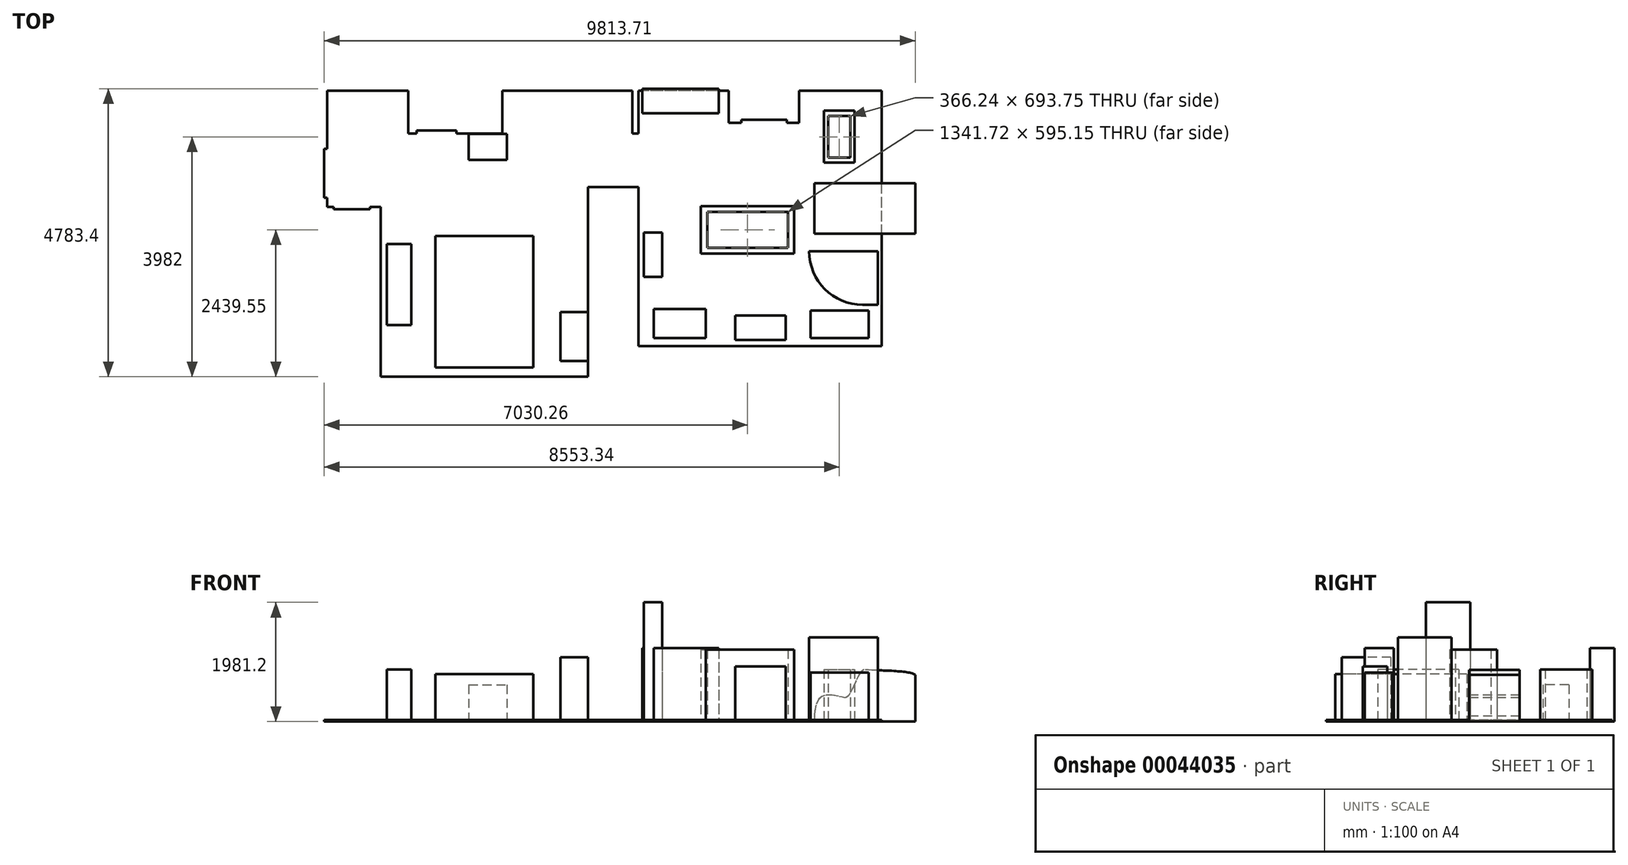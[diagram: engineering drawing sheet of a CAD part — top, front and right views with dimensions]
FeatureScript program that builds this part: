
annotation { "Feature Type Name" : "Feature", "Feature Type Description" : "" }
export const myFeature = defineFeature(function(context is Context, id is Id, definition is map)
    precondition{}
    {
        {
            var Q0;
            Q0=qCreatedBy(makeId("Top.planeOp"),FACE);
            var sketch = newSketch(context, id + "F0", { "sketchPlane" : qUnion([Q0])});
            skLineSegment(sketch, "E0.bottom", {"start": v(0, 0) * mm, "end": v(-101.6, 0) * mm});
            skLineSegment(sketch, "E0.top", {"start": v(0, 2819.4) * mm, "end": v(-101.6, 2819.4) * mm});
            skLineSegment(sketch, "E0.left", {"start": v(0, 0) * mm, "end": v(0, 2819.4) * mm});
            skLineSegment(sketch, "E0.right", {"start": v(-101.6, 0) * mm, "end": v(-101.6, 2819.4) * mm});
            skLineSegment(sketch, "E1.bottom", {"start": v(0, 0) * mm, "end": v(3441.7, 0) * mm});
            skLineSegment(sketch, "E1.top", {"start": v(0, -101.6) * mm, "end": v(3441.7, -101.6) * mm});
            skLineSegment(sketch, "E1.left", {"start": v(0, 0) * mm, "end": v(0, -101.6) * mm});
            skLineSegment(sketch, "E1.right", {"start": v(3441.7, 0) * mm, "end": v(3441.7, -101.6) * mm});
            skLineSegment(sketch, "E2.bottom", {"start": v(1485.9, 4140.2) * mm, "end": v(1917.7, 4140.2) * mm});
            skLineSegment(sketch, "E2.top", {"start": v(1485.9, 4572) * mm, "end": v(1917.7, 4572) * mm});
            skLineSegment(sketch, "E2.left", {"start": v(1485.9, 4140.2) * mm, "end": v(1485.9, 4572) * mm});
            skLineSegment(sketch, "E2.right", {"start": v(1917.7, 4140.2) * mm, "end": v(1917.7, 4572) * mm});
            skLineSegment(sketch, "E3.bottom", {"start": v(0, 2819.4) * mm, "end": v(-181.25, 2819.4) * mm});
            skLineSegment(sketch, "E3.top", {"start": v(0, 2717.8) * mm, "end": v(-990.6, 2717.8) * mm});
            skLineSegment(sketch, "E3.left", {"start": v(0, 2819.4) * mm, "end": v(0, 2717.8) * mm});
            skLineSegment(sketch, "E3.right", {"start": v(-990.6, 2819.4) * mm, "end": v(-990.6, 2717.8) * mm});
            skLineSegment(sketch, "E4.bottom", {"start": v(-990.6, 2819.4) * mm, "end": v(-889, 2819.4) * mm});
            skLineSegment(sketch, "E4.top", {"start": v(-990.6, 4495.8) * mm, "end": v(-889, 4495.8) * mm});
            skLineSegment(sketch, "E4.left", {"start": v(-990.6, 2819.4) * mm, "end": v(-990.6, 4495.8) * mm});
            skLineSegment(sketch, "E4.right", {"start": v(-889, 2819.4) * mm, "end": v(-889, 2971.8) * mm});
            skLineSegment(sketch, "E5", {"start": v(1701.8, 4140.2) * mm, "end": v(1701.8, 4749.8) * mm, "construction": true});
            skLineSegment(sketch, "E6", {"start": v(1701.8, 4749.8) * mm, "end": v(-889, 4749.8) * mm, "construction": true});
            skLineSegment(sketch, "E7.bottom", {"start": v(-889, 4495.8) * mm, "end": v(-990.6, 4495.8) * mm});
            skLineSegment(sketch, "E7.top", {"start": v(-889, 4749.8) * mm, "end": v(-990.6, 4749.8) * mm});
            skLineSegment(sketch, "E7.left", {"start": v(-889, 4495.8) * mm, "end": v(-889, 4749.8) * mm});
            skLineSegment(sketch, "E7.right", {"start": v(-990.6, 4495.8) * mm, "end": v(-990.6, 4749.8) * mm});
            skLineSegment(sketch, "E8.bottom", {"start": v(3441.7, 0) * mm, "end": v(3543.3, 0) * mm});
            skLineSegment(sketch, "E8.top", {"start": v(3441.7, 3149.6) * mm, "end": v(3543.3, 3149.6) * mm});
            skLineSegment(sketch, "E8.left", {"start": v(3441.7, 0) * mm, "end": v(3441.7, 3149.6) * mm});
            skLineSegment(sketch, "E8.right", {"start": v(3543.3, 0) * mm, "end": v(3543.3, 3149.6) * mm});
            skLineSegment(sketch, "E9.bottom", {"start": v(3441.7, 3149.6) * mm, "end": v(4279.9, 3149.6) * mm});
            skLineSegment(sketch, "E9.top", {"start": v(3441.7, 3048) * mm, "end": v(4279.9, 3048) * mm});
            skLineSegment(sketch, "E9.left", {"start": v(3441.7, 3149.6) * mm, "end": v(3441.7, 3048) * mm});
            skLineSegment(sketch, "E9.right", {"start": v(4279.9, 3149.6) * mm, "end": v(4279.9, 3048) * mm});
            skLineSegment(sketch, "E10", {"start": v(0, 0) * mm, "end": v(8318.5, 0) * mm, "construction": true});
            skLineSegment(sketch, "E11.bottom", {"start": v(4279.9, 3149.6) * mm, "end": v(4178.3, 3149.6) * mm});
            skLineSegment(sketch, "E11.top", {"start": v(4298.95, 0) * mm, "end": v(4178.3, 0) * mm});
            skLineSegment(sketch, "E11.left", {"start": v(4279.9, 3149.6) * mm, "end": v(4279.9, 406.4) * mm});
            skLineSegment(sketch, "E11.right", {"start": v(4178.3, 3149.6) * mm, "end": v(4178.3, 406.4) * mm});
            skLineSegment(sketch, "E12.bottom", {"start": v(4298.95, 0) * mm, "end": v(8337.55, 0) * mm});
            skLineSegment(sketch, "E13.bottom", {"start": v(3505.2, 1168.4) * mm, "end": v(3937, 1168.4) * mm});
            skLineSegment(sketch, "E13.top", {"start": v(3505.2, 736.6) * mm, "end": v(3937, 736.6) * mm});
            skLineSegment(sketch, "E13.left", {"start": v(3505.2, 1168.4) * mm, "end": v(3505.2, 736.6) * mm});
            skLineSegment(sketch, "E13.right", {"start": v(3937, 1168.4) * mm, "end": v(3937, 736.6) * mm});
            skLineSegment(sketch, "E14.bottom", {"start": v(4279.9, 508) * mm, "end": v(8318.5, 508) * mm});
            skLineSegment(sketch, "E14.top", {"start": v(4279.9, 406.4) * mm, "end": v(8318.5, 406.4) * mm});
            skLineSegment(sketch, "E14.left", {"start": v(4279.9, 508) * mm, "end": v(4279.9, 406.4) * mm});
            skLineSegment(sketch, "E14.right", {"start": v(8318.5, 508) * mm, "end": v(8318.5, 406.4) * mm});
            skLineSegment(sketch, "E15", {"start": v(4279.9, 406.4) * mm, "end": v(4178.3, 406.4) * mm});
            skLineSegment(sketch, "E16.bottom", {"start": v(8318.5, 508) * mm, "end": v(8420.1, 508) * mm});
            skLineSegment(sketch, "E16.top", {"start": v(8318.5, 4749.8) * mm, "end": v(8420.1, 4749.8) * mm});
            skLineSegment(sketch, "E16.left", {"start": v(8318.5, 508) * mm, "end": v(8318.5, 4749.8) * mm});
            skLineSegment(sketch, "E16.right", {"start": v(8420.1, 508) * mm, "end": v(8420.1, 4749.8) * mm});
            skLineSegment(sketch, "E17.bottom", {"start": v(8318.5, 4749.8) * mm, "end": v(6946.9, 4749.8) * mm});
            skLineSegment(sketch, "E17.top", {"start": v(8318.5, 4851.4) * mm, "end": v(6946.9, 4851.4) * mm});
            skLineSegment(sketch, "E17.left", {"start": v(8318.5, 4749.8) * mm, "end": v(8318.5, 4851.4) * mm});
            skLineSegment(sketch, "E17.right", {"start": v(6946.9, 4749.8) * mm, "end": v(6946.9, 4851.4) * mm});
            skLineSegment(sketch, "E18.bottom", {"start": v(6946.9, 4749.8) * mm, "end": v(6845.3, 4749.8) * mm});
            skLineSegment(sketch, "E18.top", {"start": v(6946.9, 4216.4) * mm, "end": v(6845.3, 4216.4) * mm});
            skLineSegment(sketch, "E18.left", {"start": v(6946.9, 4749.8) * mm, "end": v(6946.9, 4216.4) * mm});
            skLineSegment(sketch, "E18.right", {"start": v(6845.3, 4749.8) * mm, "end": v(6845.3, 4216.4) * mm});
            skLineSegment(sketch, "E19.bottom", {"start": v(6845.3, 4216.4) * mm, "end": v(6744.88, 4216.4) * mm});
            skLineSegment(sketch, "E19.top", {"start": v(6845.3, 4318) * mm, "end": v(5778.5, 4318) * mm});
            skLineSegment(sketch, "E19.left", {"start": v(6845.3, 4216.4) * mm, "end": v(6845.3, 4318) * mm});
            skLineSegment(sketch, "E19.right", {"start": v(5778.5, 4216.4) * mm, "end": v(5778.5, 4318) * mm});
            skLineSegment(sketch, "E20.bottom", {"start": v(5778.5, 4216.4) * mm, "end": v(5880.1, 4216.4) * mm});
            skLineSegment(sketch, "E20.top", {"start": v(5778.5, 4749.8) * mm, "end": v(5880.1, 4749.8) * mm});
            skLineSegment(sketch, "E20.left", {"start": v(5778.5, 4216.4) * mm, "end": v(5778.5, 4749.8) * mm});
            skLineSegment(sketch, "E20.right", {"start": v(5880.1, 4216.4) * mm, "end": v(5880.1, 4749.8) * mm});
            skLineSegment(sketch, "E21.bottom", {"start": v(5778.5, 4749.8) * mm, "end": v(4279.9, 4749.8) * mm});
            skLineSegment(sketch, "E21.top", {"start": v(5778.5, 4851.4) * mm, "end": v(4279.9, 4851.4) * mm});
            skLineSegment(sketch, "E21.left", {"start": v(5778.5, 4749.8) * mm, "end": v(5778.5, 4851.4) * mm});
            skLineSegment(sketch, "E21.right", {"start": v(4279.9, 4749.8) * mm, "end": v(4279.9, 4851.4) * mm});
            skLineSegment(sketch, "E22.bottom", {"start": v(-889, 4749.8) * mm, "end": v(4178.3, 4749.8) * mm});
            skLineSegment(sketch, "E22.top", {"start": v(-889, 4851.4) * mm, "end": v(4178.3, 4851.4) * mm});
            skLineSegment(sketch, "E22.left", {"start": v(-889, 4749.8) * mm, "end": v(-889, 4851.4) * mm});
            skLineSegment(sketch, "E22.right", {"start": v(4178.3, 4749.8) * mm, "end": v(4178.3, 4851.4) * mm});
            skLineSegment(sketch, "E23.bottom", {"start": v(4279.9, 4851.4) * mm, "end": v(4178.3, 4851.4) * mm});
            skLineSegment(sketch, "E23.top", {"start": v(4279.9, 4038.6) * mm, "end": v(4178.3, 4038.6) * mm});
            skLineSegment(sketch, "E23.left", {"start": v(4279.9, 4851.4) * mm, "end": v(4279.9, 4038.6) * mm});
            skLineSegment(sketch, "E23.right", {"start": v(4178.3, 4851.4) * mm, "end": v(4178.3, 4038.6) * mm});
            skLineSegment(sketch, "E24", {"start": v(1798.14, 4140.2) * mm, "end": v(1798.14, 4038.6) * mm, "construction": true});
            skLineSegment(sketch, "E25", {"start": v(1798.14, 4038.6) * mm, "end": v(4178.3, 4038.6) * mm, "construction": true});
            skLineSegment(sketch, "E26", {"start": v(4178.3, 4038.6) * mm, "end": v(1798.14, 4038.6) * mm, "construction": true});
            skLineSegment(sketch, "E27", {"start": v(1798.14, 4038.6) * mm, "end": v(-889, 4038.6) * mm, "construction": true});
            skLineSegment(sketch, "E28.bottom", {"start": v(1397, 4749.8) * mm, "end": v(1485.9, 4749.8) * mm});
            skLineSegment(sketch, "E28.top", {"start": v(1397, 4038.6) * mm, "end": v(1485.9, 4038.6) * mm});
            skLineSegment(sketch, "E28.left", {"start": v(1397, 4749.8) * mm, "end": v(1397, 4038.6) * mm});
            skLineSegment(sketch, "E28.right", {"start": v(1485.9, 4749.8) * mm, "end": v(1485.9, 4038.6) * mm});
            skLineSegment(sketch, "E29.bottom", {"start": v(1917.7, 4749.8) * mm, "end": v(2019.3, 4749.8) * mm});
            skLineSegment(sketch, "E29.top", {"start": v(1917.7, 4038.6) * mm, "end": v(2019.3, 4038.6) * mm});
            skLineSegment(sketch, "E29.left", {"start": v(1917.7, 4749.8) * mm, "end": v(1917.7, 4038.6) * mm});
            skLineSegment(sketch, "E29.right", {"start": v(2019.3, 4749.8) * mm, "end": v(2019.3, 4038.6) * mm});
            skLineSegment(sketch, "E30.bottom", {"start": v(1397, 4038.6) * mm, "end": v(2019.3, 4038.6) * mm});
            skLineSegment(sketch, "E30.top", {"start": v(1397, 4140.2) * mm, "end": v(2019.3, 4140.2) * mm});
            skLineSegment(sketch, "E30.left", {"start": v(1397, 4038.6) * mm, "end": v(1397, 4140.2) * mm});
            skLineSegment(sketch, "E30.right", {"start": v(2019.3, 4038.6) * mm, "end": v(2019.3, 4140.2) * mm});
            skLineSegment(sketch, "E31.bottom", {"start": v(1295.4, 4038.6) * mm, "end": v(1257.3, 4038.6) * mm});
            skLineSegment(sketch, "E31.top", {"start": v(1295.4, 4140.2) * mm, "end": v(1257.3, 4140.2) * mm});
            skLineSegment(sketch, "E31.left", {"start": v(1295.4, 4038.6) * mm, "end": v(1295.4, 4140.2) * mm});
            skLineSegment(sketch, "E31.right", {"start": v(1257.3, 4038.6) * mm, "end": v(1257.3, 4140.2) * mm});
            skLineSegment(sketch, "E32.bottom", {"start": v(558.8, 4038.6) * mm, "end": v(596.9, 4038.6) * mm});
            skLineSegment(sketch, "E32.top", {"start": v(558.8, 4140.2) * mm, "end": v(596.9, 4140.2) * mm});
            skLineSegment(sketch, "E32.left", {"start": v(558.8, 4038.6) * mm, "end": v(558.8, 4140.2) * mm});
            skLineSegment(sketch, "E32.right", {"start": v(596.9, 4038.6) * mm, "end": v(596.9, 4140.2) * mm});
            skLineSegment(sketch, "E33.bottom", {"start": v(558.8, 4038.6) * mm, "end": v(457.2, 4038.6) * mm});
            skLineSegment(sketch, "E33.top", {"start": v(558.8, 4749.8) * mm, "end": v(457.2, 4749.8) * mm});
            skLineSegment(sketch, "E33.left", {"start": v(558.8, 4038.6) * mm, "end": v(558.8, 4749.8) * mm});
            skLineSegment(sketch, "E33.right", {"start": v(457.2, 4038.6) * mm, "end": v(457.2, 4749.8) * mm});
            skLineSegment(sketch, "E34", {"start": v(1295.4, 4038.6) * mm, "end": v(1397, 4038.6) * mm});
            skLineSegment(sketch, "E35", {"start": v(596.9, 4089.4) * mm, "end": v(1257.3, 4089.4) * mm});
            skLineSegment(sketch, "E36", {"start": v(5984.67, 4216.4) * mm, "end": v(5984.67, 4267.2) * mm});
            skPoint(sketch, "E36.endSnap0", {"position": v(5778.5, 4267.2) * mm});
            skLineSegment(sketch, "E37", {"start": v(5984.67, 4267.2) * mm, "end": v(6744.88, 4267.2) * mm});
            skLineSegment(sketch, "E38", {"start": v(6744.88, 4267.2) * mm, "end": v(6744.88, 4216.4) * mm});
            skLineSegment(sketch, "E39.trimOffspring", {"start": v(5984.67, 4216.4) * mm, "end": v(5778.5, 4216.4) * mm});
            skLineSegment(sketch, "E40", {"start": v(-784.2, 2819.4) * mm, "end": v(-784.2, 2780.53) * mm});
            skLineSegment(sketch, "E41", {"start": v(-784.2, 2780.53) * mm, "end": v(-181.25, 2782.63) * mm});
            skLineSegment(sketch, "E42", {"start": v(-181.25, 2782.63) * mm, "end": v(-181.25, 2819.4) * mm});
            skLineSegment(sketch, "E43.trimOffspring", {"start": v(-784.2, 2819.4) * mm, "end": v(-990.6, 2819.4) * mm});
            skLineSegment(sketch, "E44", {"start": v(-889, 2971.8) * mm, "end": v(-939.8, 2971.8) * mm});
            skLineSegment(sketch, "E45", {"start": v(-939.8, 2971.8) * mm, "end": v(-939.8, 3784.6) * mm});
            skLineSegment(sketch, "E46", {"start": v(-939.8, 3784.6) * mm, "end": v(-889, 3784.6) * mm});
            skLineSegment(sketch, "E47.trimOffspring", {"start": v(-889, 3784.6) * mm, "end": v(-889, 4495.8) * mm});
            skSolve(sketch);
        }
        {
            var Q0;
            Q0=makeQuery(id+"F0.imprint","IMPRINT",FACE,{"disambiguationData":[TD([[makeQuery(id+"F0.imprint","IMPRINT",EDGE,{"derivedFrom":sQuery(id+"F0.wireOp",EDGE,"E0.left")}),-1.0]])]});
            extrude(context, id + "F1", {"entities" : qUnion([Q0]), "depth" : 25.4 * mm});
        }
        {
            var Q0;
            Q0=makeQuery(id+"F1.opExtrude","CAP_FACE",FACE,{"disambiguationData":[OSD([sQuery(id+"F0.wireOp",EDGE,"E0.left"),sQuery(id+"F0.wireOp",EDGE,"E1.bottom"),sQuery(id+"F0.wireOp",EDGE,"E2.bottom"),sQuery(id+"F0.wireOp",EDGE,"E2.top"),sQuery(id+"F0.wireOp",EDGE,"E2.left"),sQuery(id+"F0.wireOp",EDGE,"E2.right"),sQuery(id+"F0.wireOp",EDGE,"E3.bottom"),sQuery(id+"F0.wireOp",EDGE,"E3.left"),sQuery(id+"F0.wireOp",EDGE,"E4.right"),sQuery(id+"F0.wireOp",EDGE,"E7.left"),sQuery(id+"F0.wireOp",EDGE,"E8.left"),sQuery(id+"F0.wireOp",EDGE,"E9.bottom"),sQuery(id+"F0.wireOp",EDGE,"E9.left"),sQuery(id+"F0.wireOp",EDGE,"E11.bottom"),sQuery(id+"F0.wireOp",EDGE,"E11.left"),sQuery(id+"F0.wireOp",EDGE,"E14.bottom"),sQuery(id+"F0.wireOp",EDGE,"E16.left"),sQuery(id+"F0.wireOp",EDGE,"E17.bottom"),sQuery(id+"F0.wireOp",EDGE,"E18.top"),sQuery(id+"F0.wireOp",EDGE,"E18.left"),sQuery(id+"F0.wireOp",EDGE,"E19.bottom"),sQuery(id+"F0.wireOp",EDGE,"E20.bottom"),sQuery(id+"F0.wireOp",EDGE,"E20.left"),sQuery(id+"F0.wireOp",EDGE,"E21.bottom"),sQuery(id+"F0.wireOp",EDGE,"E22.bottom"),sQuery(id+"F0.wireOp",EDGE,"E23.top"),sQuery(id+"F0.wireOp",EDGE,"E23.left"),sQuery(id+"F0.wireOp",EDGE,"E23.right")])],"isStart":false});
            var sketch = newSketch(context, id + "F2", { "sketchPlane" : qUnion([Q0])});
            skLineSegment(sketch, "E48.bottom", {"start": v(908.05, 2336.8) * mm, "end": v(2533.65, 2336.8) * mm});
            skLineSegment(sketch, "E48.top", {"start": v(908.05, 152.4) * mm, "end": v(2533.65, 152.4) * mm});
            skLineSegment(sketch, "E48.left", {"start": v(908.05, 2336.8) * mm, "end": v(908.05, 152.4) * mm});
            skLineSegment(sketch, "E48.right", {"start": v(2533.65, 2336.8) * mm, "end": v(2533.65, 152.4) * mm});
            skLineSegment(sketch, "E49.0", {"start": v(0, 0) * mm, "end": v(3441.7, 0) * mm});
            skPoint(sketch, "E50", {"position": v(1720.85, 0) * mm});
            skPoint(sketch, "E51", {"position": v(1720.85, 152.4) * mm});
            skSolve(sketch);
        }
        {
            var Q0;
            Q0 = qSketchRegion(id + "F2", true);
            extrude(context, id + "F3", {"entities" : qUnion([Q0]), "depth" : 762 * mm});
        }
        {
            var Q0;
            Q0=qCreatedBy(makeId("Top.planeOp"),FACE);
            var sketch = newSketch(context, id + "F4", { "sketchPlane" : qUnion([Q0])});
            skLineSegment(sketch, "E52.bottom", {"start": v(4339.31, 4783.4) * mm, "end": v(5609.31, 4783.4) * mm});
            skLineSegment(sketch, "E52.top", {"start": v(4339.31, 4377) * mm, "end": v(5609.31, 4377) * mm});
            skLineSegment(sketch, "E52.left", {"start": v(4339.31, 4783.4) * mm, "end": v(4339.31, 4377) * mm});
            skLineSegment(sketch, "E52.right", {"start": v(5609.31, 4783.4) * mm, "end": v(5609.31, 4377) * mm});
            skSolve(sketch);
        }
        {
            var Q0;
            Q0 = qSketchRegion(id + "F4", true);
            extrude(context, id + "F5", {"entities" : qUnion([Q0]), "depth" : 1219.2 * mm});
        }
        {
            var Q0;
            Q0=qCreatedBy(makeId("Top.planeOp"),FACE);
            var sketch = newSketch(context, id + "F6", { "sketchPlane" : qUnion([Q0])});
            skLineSegment(sketch, "E53.bottom", {"start": v(8104.33, 639.74) * mm, "end": v(7139.13, 639.74) * mm});
            skLineSegment(sketch, "E53.top", {"start": v(8104.33, 1096.94) * mm, "end": v(7139.13, 1096.94) * mm});
            skLineSegment(sketch, "E53.left", {"start": v(8104.33, 639.74) * mm, "end": v(8104.33, 1096.94) * mm});
            skLineSegment(sketch, "E53.right", {"start": v(7139.13, 639.74) * mm, "end": v(7139.13, 1096.94) * mm});
            skSolve(sketch);
        }
        {
            var Q0;
            Q0 = qSketchRegion(id + "F6", true);
            extrude(context, id + "F7", {"entities" : qUnion([Q0]), "depth" : 812.8 * mm});
        }
        {
            var Q0;
            Q0=qCreatedBy(makeId("Top.planeOp"),FACE);
            var sketch = newSketch(context, id + "F8", { "sketchPlane" : qUnion([Q0])});
            skLineSegment(sketch, "E54.bottom", {"start": v(8255.57, 1194.17) * mm, "end": v(8001.57, 1194.17) * mm});
            skLineSegment(sketch, "E54.top", {"start": v(8255.57, 2083.17) * mm, "end": v(8001.57, 2083.17) * mm});
            skLineSegment(sketch, "E54.left", {"start": v(8255.57, 1194.17) * mm, "end": v(8255.57, 2083.17) * mm});
            skLineSegment(sketch, "E54.right", {"start": v(8001.57, 1194.17) * mm, "end": v(8001.57, 2083.17) * mm});
            skLineSegment(sketch, "E55", {"start": v(8255.57, 2083.17) * mm, "end": v(7112.57, 2083.17) * mm});
            skArc(sketch, "E56", {"start": v(7112.57, 2083.17) * mm, "mid": v(7372.95, 1454.55) * mm, "end": v(8001.57, 1194.17) * mm});
            skSolve(sketch);
        }
        {
            var Q0;
            Q0 = qSketchRegion(id + "F8", true);
            extrude(context, id + "F9", {"entities" : qUnion([Q0]), "depth" : 1397 * mm});
        }
        {
            var Q0;
            Q0=qCreatedBy(makeId("Top.planeOp"),FACE);
            var sketch = newSketch(context, id + "F10", { "sketchPlane" : qUnion([Q0])});
            skLineSegment(sketch, "E57.bottom", {"start": v(4531.26, 639.74) * mm, "end": v(5394.86, 639.74) * mm});
            skLineSegment(sketch, "E57.top", {"start": v(4531.26, 1122.34) * mm, "end": v(5394.86, 1122.34) * mm});
            skLineSegment(sketch, "E57.left", {"start": v(4531.26, 639.74) * mm, "end": v(4531.26, 1122.34) * mm});
            skLineSegment(sketch, "E57.right", {"start": v(5394.86, 639.74) * mm, "end": v(5394.86, 1122.34) * mm});
            skSolve(sketch);
        }
        {
            var Q0;
            Q0 = qSketchRegion(id + "F10", true);
            extrude(context, id + "F11", {"entities" : qUnion([Q0]), "depth" : 1219.2 * mm});
        }
        {
            var Q0;
            Q0=qCreatedBy(makeId("Top.planeOp"),FACE);
            var sketch = newSketch(context, id + "F12", { "sketchPlane" : qUnion([Q0])});
            skLineSegment(sketch, "E58.bottom", {"start": v(1460.8, 4028.5) * mm, "end": v(2095.8, 4028.5) * mm});
            skLineSegment(sketch, "E58.top", {"start": v(1460.8, 3596.7) * mm, "end": v(2095.8, 3596.7) * mm});
            skLineSegment(sketch, "E58.left", {"start": v(1460.8, 4028.5) * mm, "end": v(1460.8, 3596.7) * mm});
            skLineSegment(sketch, "E58.right", {"start": v(2095.8, 4028.5) * mm, "end": v(2095.8, 3596.7) * mm});
            skSolve(sketch);
        }
        {
            var Q0;
            Q0 = qSketchRegion(id + "F12", true);
            extrude(context, id + "F13", {"entities" : qUnion([Q0]), "depth" : 609.6 * mm});
        }
        {
            var Q0;
            Q0=qCreatedBy(makeId("Top.planeOp"),FACE);
            var sketch = newSketch(context, id + "F14", { "sketchPlane" : qUnion([Q0])});
            skLineSegment(sketch, "E59.bottom", {"start": v(4370.2, 2392.8) * mm, "end": v(4675, 2392.8) * mm});
            skLineSegment(sketch, "E59.top", {"start": v(4370.2, 1656.2) * mm, "end": v(4675, 1656.2) * mm});
            skLineSegment(sketch, "E59.left", {"start": v(4370.2, 2392.8) * mm, "end": v(4370.2, 1656.2) * mm});
            skLineSegment(sketch, "E59.right", {"start": v(4675, 2392.8) * mm, "end": v(4675, 1656.2) * mm});
            skSolve(sketch);
        }
        {
            var Q0;
            Q0 = qSketchRegion(id + "F14", true);
            extrude(context, id + "F15", {"entities" : qUnion([Q0]), "depth" : 1981.2 * mm});
        }
        {
            var Q0;
            Q0=qCreatedBy(makeId("Top.planeOp"),FACE);
            var sketch = newSketch(context, id + "F16", { "sketchPlane" : qUnion([Q0])});
            skLineSegment(sketch, "E60.bottom", {"start": v(3438.11, 1072.66) * mm, "end": v(2980.91, 1072.66) * mm});
            skLineSegment(sketch, "E60.top", {"start": v(3438.11, 259.86) * mm, "end": v(2980.91, 259.86) * mm});
            skLineSegment(sketch, "E60.left", {"start": v(3438.11, 1072.66) * mm, "end": v(3438.11, 259.86) * mm});
            skLineSegment(sketch, "E60.right", {"start": v(2980.91, 1072.66) * mm, "end": v(2980.91, 259.86) * mm});
            skSolve(sketch);
        }
        {
            var Q0;
            Q0 = qSketchRegion(id + "F16", true);
            extrude(context, id + "F17", {"entities" : qUnion([Q0]), "depth" : 1066.8 * mm});
        }
        {
            var Q0;
            Q0=qCreatedBy(makeId("Top.planeOp"),FACE);
            var sketch = newSketch(context, id + "F18", { "sketchPlane" : qUnion([Q0])});
            skLineSegment(sketch, "E61.bottom", {"start": v(100.12, 2201.56) * mm, "end": v(506.52, 2201.56) * mm});
            skLineSegment(sketch, "E61.top", {"start": v(100.12, 855.36) * mm, "end": v(506.52, 855.36) * mm});
            skLineSegment(sketch, "E61.left", {"start": v(100.12, 2201.56) * mm, "end": v(100.12, 855.36) * mm});
            skLineSegment(sketch, "E61.right", {"start": v(506.52, 2201.56) * mm, "end": v(506.52, 855.36) * mm});
            skSolve(sketch);
        }
        {
            var Q0;
            Q0 = qSketchRegion(id + "F18", true);
            extrude(context, id + "F19", {"entities" : qUnion([Q0]), "depth" : 863.6 * mm});
        }
        {
            var Q0;
            Q0=qCreatedBy(makeId("Top.planeOp"),FACE);
            var sketch = newSketch(context, id + "F20", { "sketchPlane" : qUnion([Q0])});
            skLineSegment(sketch, "E62.bottom", {"start": v(5886.53, 1015.34) * mm, "end": v(6724.73, 1015.34) * mm});
            skLineSegment(sketch, "E62.top", {"start": v(5886.53, 608.94) * mm, "end": v(6724.73, 608.94) * mm});
            skLineSegment(sketch, "E62.left", {"start": v(5886.53, 1015.34) * mm, "end": v(5886.53, 608.94) * mm});
            skLineSegment(sketch, "E62.right", {"start": v(6724.73, 1015.34) * mm, "end": v(6724.73, 608.94) * mm});
            skSolve(sketch);
        }
        {
            var Q0;
            Q0 = qSketchRegion(id + "F20", true);
            extrude(context, id + "F21", {"entities" : qUnion([Q0]), "depth" : 914.4 * mm});
        }
        {
            var Q0;
            Q0=qCreatedBy(makeId("Top.planeOp"),FACE);
            var sketch = newSketch(context, id + "F22", { "sketchPlane" : qUnion([Q0])});
            skLineSegment(sketch, "E63.bottom", {"start": v(5311.57, 2046.35) * mm, "end": v(6860.97, 2046.35) * mm});
            skLineSegment(sketch, "E63.top", {"start": v(5311.57, 2833.75) * mm, "end": v(6860.97, 2833.75) * mm});
            skLineSegment(sketch, "E63.left", {"start": v(5311.57, 2046.35) * mm, "end": v(5311.57, 2833.75) * mm});
            skLineSegment(sketch, "E63.right", {"start": v(6860.97, 2046.35) * mm, "end": v(6860.97, 2833.75) * mm});
            skLineSegment(sketch, "E64.bottom", {"start": v(5419.6, 2141.98) * mm, "end": v(6761.32, 2141.98) * mm});
            skLineSegment(sketch, "E64.top", {"start": v(5419.6, 2737.12) * mm, "end": v(6761.32, 2737.12) * mm});
            skLineSegment(sketch, "E64.left", {"start": v(5419.6, 2141.98) * mm, "end": v(5419.6, 2737.12) * mm});
            skLineSegment(sketch, "E64.right", {"start": v(6761.32, 2141.98) * mm, "end": v(6761.32, 2737.12) * mm});
            skSolve(sketch);
        }
        {
            var Q0;
            Q0 = qSketchRegion(id + "F22", true);
            extrude(context, id + "F23", {"entities" : qUnion([Q0]), "depth" : 1193.8 * mm});
        }
        {
            var Q0;
            Q0=qCreatedBy(makeId("Top.planeOp"),FACE);
            var sketch = newSketch(context, id + "F24", { "sketchPlane" : qUnion([Q0])});
            skLineSegment(sketch, "E65.bottom", {"start": v(7360.1, 4419.23) * mm, "end": v(7868.1, 4419.23) * mm});
            skLineSegment(sketch, "E65.top", {"start": v(7360.1, 3555.63) * mm, "end": v(7868.1, 3555.63) * mm});
            skLineSegment(sketch, "E65.left", {"start": v(7360.1, 4419.23) * mm, "end": v(7360.1, 3555.63) * mm});
            skLineSegment(sketch, "E65.right", {"start": v(7868.1, 4419.23) * mm, "end": v(7868.1, 3555.63) * mm});
            skLineSegment(sketch, "E66.bottom", {"start": v(7430.42, 4328.88) * mm, "end": v(7796.67, 4328.88) * mm});
            skLineSegment(sketch, "E66.top", {"start": v(7430.42, 3635.13) * mm, "end": v(7796.67, 3635.13) * mm});
            skLineSegment(sketch, "E66.left", {"start": v(7430.42, 4328.88) * mm, "end": v(7430.42, 3635.13) * mm});
            skLineSegment(sketch, "E66.right", {"start": v(7796.67, 4328.88) * mm, "end": v(7796.67, 3635.13) * mm});
            skSolve(sketch);
        }
        {
            var Q0;
            Q0 = qSketchRegion(id + "F24", true);
            extrude(context, id + "F25", {"entities" : qUnion([Q0]), "depth" : 863.6 * mm});
        }
        {
            var Q0;
            Q0=qCreatedBy(makeId("Top.planeOp"),FACE);
            var sketch = newSketch(context, id + "F26", { "sketchPlane" : qUnion([Q0])});
            skLineSegment(sketch, "E67.bottom", {"start": v(7197.51, 3213.87) * mm, "end": v(8873.91, 3213.87) * mm});
            skLineSegment(sketch, "E67.top", {"start": v(7197.51, 2375.67) * mm, "end": v(8873.91, 2375.67) * mm});
            skLineSegment(sketch, "E67.left", {"start": v(7197.51, 3213.87) * mm, "end": v(7197.51, 2375.67) * mm});
            skLineSegment(sketch, "E67.right", {"start": v(8873.91, 3213.87) * mm, "end": v(8873.91, 2375.67) * mm});
            skSolve(sketch);
        }
        {
            var Q0;
            Q0 = qSketchRegion(id + "F26", true);
            extrude(context, id + "F27", {"entities" : qUnion([Q0]), "depth" : 914.4 * mm});
        }
        {
            var Q0;
            Q0=makeQuery(id+"F27.opExtrude","SWEPT_FACE",FACE,{"disambiguationData":[OSD([sQuery(id+"F26.wireOp",EDGE,"E67.bottom")])]});
            var sketch = newSketch(context, id + "F28", { "sketchPlane" : qUnion([Q0])});
            skFitSpline(sketch, "E68", {"points": [v(-8873.91, 779.97) * mm, v(-8105.4, 858.3) * mm, v(-7960.1, 814.01) * mm, v(-7753.4, 418.83) * mm, v(-7641.31, 410.84) * mm, v(-7311.71, 412.37) * mm, v(-7197.51, 95.6) * mm], "startDerivative": vector(797.05, 766.58) * mm, "endDerivative": vector(212.66, -1999.7) * mm});
            skLineSegment(sketch, "E69.0", {"start": v(-8873.91, 914.4) * mm, "end": v(-8873.91, 779.97) * mm});
            skLineSegment(sketch, "E70.0", {"start": v(-7197.51, 914.4) * mm, "end": v(-7197.51, 95.6) * mm});
            skLineSegment(sketch, "E71.0", {"start": v(-7197.51, 914.4) * mm, "end": v(-8873.91, 914.4) * mm});
            skPoint(sketch, "E72.start.orphan", {"position": v(-8873.91, 0) * mm});
            skPoint(sketch, "E73.orphan", {"position": v(-7197.51, 0) * mm});
            skSolve(sketch);
        }
        {
            var Q0;
            Q0 = qSketchRegion(id + "F28", true);
            extrude(context, id + "F29", {"entities" : qUnion([Q0]), "operationType" : NewBodyOperationType.REMOVE, "endBound" : BoundingType.UP_TO_NEXT, "oppositeDirection" : true, "depth" : 25.4 * mm});
        }
    });
